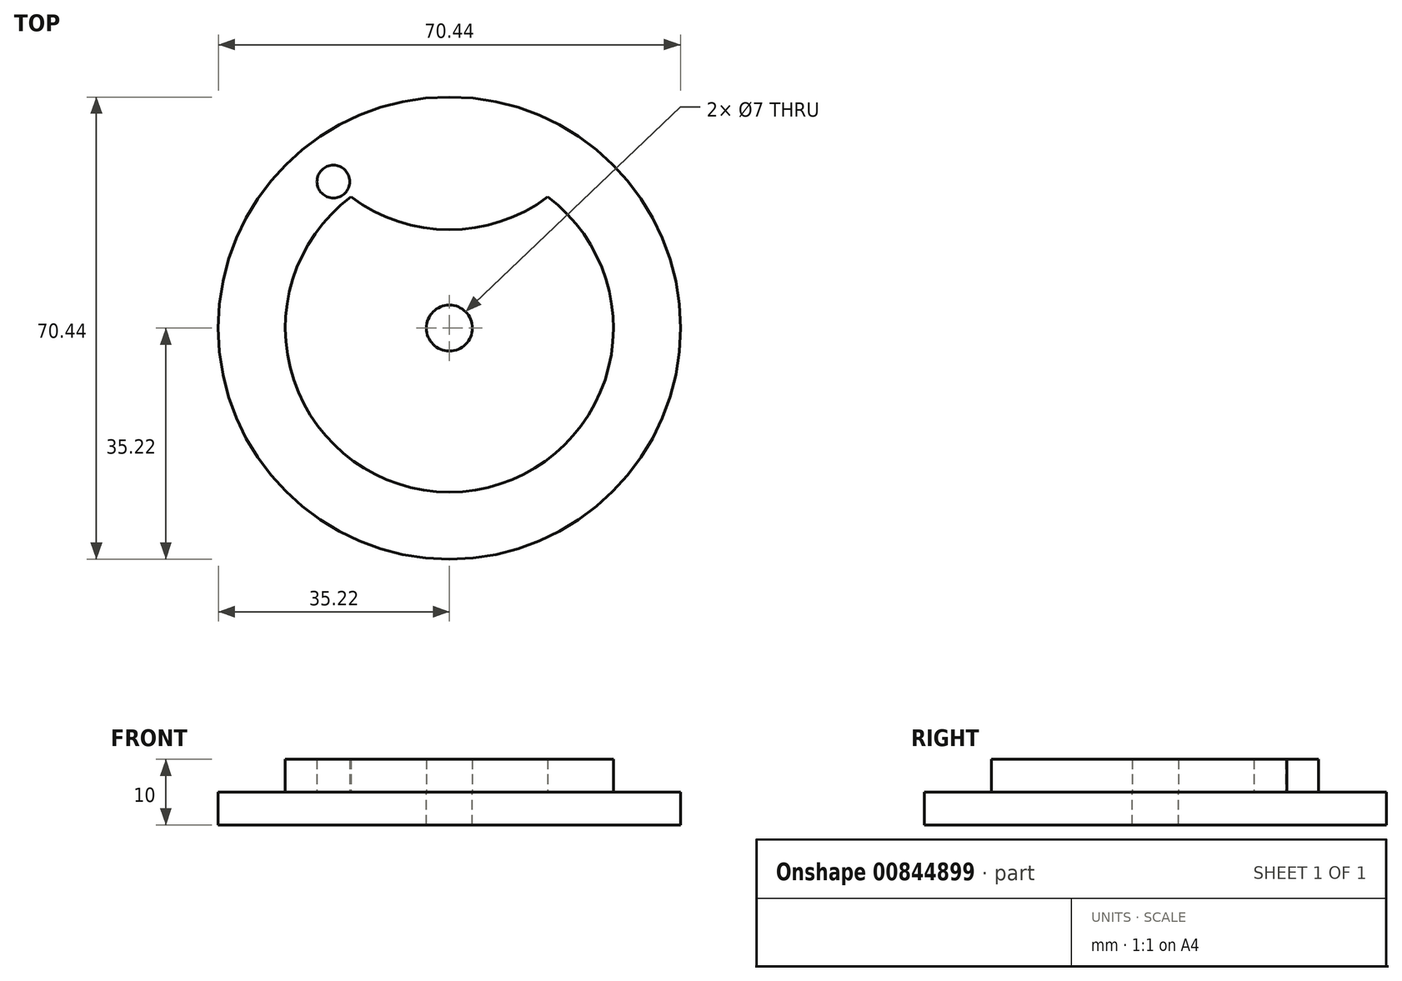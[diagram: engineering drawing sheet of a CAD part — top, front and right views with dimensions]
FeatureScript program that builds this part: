
annotation { "Feature Type Name" : "Feature", "Feature Type Description" : "" }
export const myFeature = defineFeature(function(context is Context, id is Id, definition is map)
    precondition{}
    {
        {
            var Q0;
            Q0=qCreatedBy(makeId("Top.planeOp"),FACE);
            var sketch = newSketch(context, id + "F0", { "sketchPlane" : qUnion([Q0])});
            skArc(sketch, "E0", {"start": v(-15, 20) * mm, "mid": v(0, -25) * mm, "end": v(15, 20) * mm});
            skArc(sketch, "E1", {"start": v(15, 20) * mm, "mid": v(0, 25) * mm, "end": v(-15, 20) * mm});
            skArc(sketch, "E2.1.0", {"start": v(20, 55) * mm, "mid": v(15, 40) * mm, "end": v(20, 25) * mm});
            skArc(sketch, "E2.2.0", {"start": v(-15, 60) * mm, "mid": v(0, 55) * mm, "end": v(15, 60) * mm});
            skArc(sketch, "E2.3.0", {"start": v(-20, 25) * mm, "mid": v(-15, 40) * mm, "end": v(-20, 55) * mm});
            skPoint(sketch, "E2.center", {"position": v(0, 40) * mm});
            skLineSegment(sketch, "E3", {"start": v(-19.98, 24.97) * mm, "end": v(15.03, 59.98) * mm});
            skLineSegment(sketch, "E4", {"start": v(-19.98, 55.03) * mm, "end": v(15.03, 20.02) * mm});
            skLineSegment(sketch, "E5", {"start": v(19.98, 24.97) * mm, "end": v(-15.03, 59.98) * mm});
            skLineSegment(sketch, "E6", {"start": v(19.98, 55.03) * mm, "end": v(-15.03, 20.02) * mm});
            skLineSegment(sketch, "E7", {"start": v(0, 44.95) * mm, "end": v(0, 35.05) * mm, "construction": true});
            skArc(sketch, "E8", {"start": v(-7.78, 27.27) * mm, "mid": v(-7.78, 32.22) * mm, "end": v(-12.73, 32.22) * mm});
            skArc(sketch, "E9", {"start": v(-12.73, 47.78) * mm, "mid": v(-7.78, 47.78) * mm, "end": v(-7.78, 52.73) * mm});
            skArc(sketch, "E10", {"start": v(7.78, 52.73) * mm, "mid": v(7.78, 47.78) * mm, "end": v(12.73, 47.78) * mm});
            skArc(sketch, "E11", {"start": v(12.73, 32.22) * mm, "mid": v(7.78, 32.22) * mm, "end": v(7.78, 27.27) * mm});
            skCircle(sketch, "E12", {"center": v(0, 40) * mm, "radius": 3.5 * mm});
            skCircle(sketch, "E13", {"center": v(0, 0) * mm, "radius": 3.5 * mm});
            skCircle(sketch, "E14", {"center": v(0, 40) * mm, "radius": 11 * mm, "construction": true});
            skLineSegment(sketch, "E15", {"start": v(0, 40) * mm, "end": v(-17.68, 22.32) * mm, "construction": true});
            skCircle(sketch, "E16", {"center": v(-17.68, 22.32) * mm, "radius": 2.5 * mm});
            skArc(sketch, "E17", {"start": v(-15, 20) * mm, "mid": v(0, 15) * mm, "end": v(15, 20) * mm});
            skArc(sketch, "E18", {"start": v(15, 20) * mm, "mid": v(0, 65) * mm, "end": v(-15, 20) * mm});
            skLineSegment(sketch, "E19", {"start": v(-19.7, 20.84) * mm, "end": v(-2.82, -2.08) * mm});
            skLineSegment(sketch, "E20", {"start": v(-15.77, 23.94) * mm, "end": v(2.67, 2.27) * mm});
            skLineSegment(sketch, "E21", {"start": v(-17.68, 22.32) * mm, "end": v(0, 0) * mm, "construction": true});
            skSolve(sketch);
        }
        {
            var Q0;
            {var subQ1=sQuery(id+"F0.wireOp",EDGE,"E0");Q0=makeQuery(id+"F0.imprint","IMPRINT",FACE,{"disambiguationData":[TD([[makeQuery(id+"F0.imprint","IMPRINT",EDGE,{"derivedFrom":subQ1}),1.0]])]});}
            var Q1;
            {var subQ0=sQuery(id+"F0.wireOp",EDGE,"E16");var subQ1=makeQuery(id+"F0.imprint","INTERSECT",VERTEX,{"derivedFrom":[subQ0,sQuery(id+"F0.wireOp",EDGE,"E20")]});Q1=makeQuery(id+"F0.imprint","IMPRINT",FACE,{"disambiguationData":[TD([[makeQuery(id+"F0.imprint","IMPRINT",EDGE,{"disambiguationData":[TD([[subQ1,-1.0]])],"derivedFrom":subQ0}),1.0]])]});}
            var Q2;
            {var subQ0=sQuery(id+"F0.wireOp",EDGE,"E16");var subQ1=makeQuery(id+"F0.imprint","INTERSECT",VERTEX,{"derivedFrom":[subQ0,sQuery(id+"F0.wireOp",EDGE,"E19")]});Q2=makeQuery(id+"F0.imprint","IMPRINT",FACE,{"disambiguationData":[TD([[makeQuery(id+"F0.imprint","IMPRINT",EDGE,{"disambiguationData":[TD([[subQ1,1.0]])],"derivedFrom":subQ0}),1.0]])]});}
            extrude(context, id + "F1", {"entities" : qUnion([Q0, Q1, Q2]), "offsetDistance" : 25 * mm, "depth" : 5 * mm});
        }
        {
            var Q0;
            Q0=makeQuery(id+"F1.opExtrude","CAP_FACE",FACE,{"disambiguationData":[OSD([sQuery(id+"F0.wireOp",EDGE,"E0"),sQuery(id+"F0.wireOp",EDGE,"E13"),sQuery(id+"F0.wireOp",EDGE,"E17")])],"isStart":true});
            var sketch = newSketch(context, id + "F2", { "sketchPlane" : qUnion([Q0])});
            skCircle(sketch, "E22", {"center": v(0, 0) * mm, "radius": 35.22 * mm});
            skSolve(sketch);
        }
        {
            var Q0;
            Q0=makeQuery(id+"F2.imprint","IMPRINT",FACE,{"disambiguationData":[TD([[makeQuery(id+"F2.imprint","IMPRINT",EDGE,{"derivedFrom":makeQuery(id+"F1.opExtrude","CAP_EDGE",EDGE,{"disambiguationData":[OSD([sQuery(id+"F0.wireOp",EDGE,"E0")])],"isStart":true})}),-1.0]])]});
            var Q1;
            Q1=makeQuery(id+"F2.imprint","IMPRINT",FACE,{"disambiguationData":[TD([[makeQuery(id+"F2.imprint","IMPRINT",EDGE,{"derivedFrom":sQuery(id+"F2.wireOp",EDGE,"E22")}),1.0]])]});
            extrude(context, id + "F3", {"entities" : qUnion([Q0, Q1]), "depth" : 5 * mm, "offsetDistance" : 25 * mm});
        }
    });
